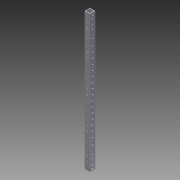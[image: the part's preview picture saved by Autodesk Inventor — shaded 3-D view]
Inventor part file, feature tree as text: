
AUTODESK INVENTOR PART (.ipt)
format: ipt  version: 2013 (Build 170138000, 138)  size: 201,728 bytes
history: native  units: in
note: dims shown in document units (in); Inventor stores cm internally (conversion verified against a paired STEP export)
features: extrude x4, sketch x4, reference x4
ambient origin geometry x8: Origin, YZ Plane, XZ Plane, XY Plane, X Axis, Y Axis, Z Axis, Center Point
bodies: Solid1 (feature_tree)
feature tree (12):
  extrude  "Extrusion1"  Depth=1.0in
  extrude  "Extrusion2"  Depth=26.0in TaperAngle=0.0deg
  extrude  "Extrusion3"  Depth=1.5in
  extrude  "Extrusion4"  Depth=9.4488in
  sketch  "Sketch1"  dims[d0=1.0in d1=1.0in]
  sketch  "Sketch2"  dims[d2=0.125in d3=26.0in d4=0.0in]
  sketch  "Sketch3"  dims[d5=0.225in d6=1.5in]
  reference  "Reference5"
  reference  "Reference6"
  reference  "Reference7"
  reference  "Reference8"
  sketch  "Sketch4"  dims[d7=26.0in d8=9.4488in d10=1.0in d11=0.3937in d13=1.0in d15=1.0in d16=0.0in d17=0.26in d25=1.0in d26=0.0in d27=0.26in d28=0.26in d29=4.25in d30=4.25in d31=17.5in d32=1.25in d33=0.26in d34=6.2992in d36=1.0in d37=0.3937in d39=1.0in d41=1.0in d42=0.75in d43=0.26in d45=1.0in d46=0.75in d47=1.0in d48=0.0in]
